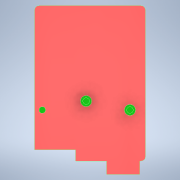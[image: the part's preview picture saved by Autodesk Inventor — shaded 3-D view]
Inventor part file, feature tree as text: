
AUTODESK INVENTOR PART (.ipt)
format: ipt  version: 2022 (Build 260153000, 153)  size: 167,424 bytes
history: native  units: mm
features: extrude x6, sketch x4, fillet x1
ambient origin geometry x8: Origin, YZ Plane, XZ Plane, XY Plane, X Axis, Y Axis, Z Axis, Center Point
bodies: Body1 (feature_tree)
feature tree (11):
  extrude  "Extrusion3"  Depth=70.0mm
  fillet  "Fillet1"  Radius=6.0mm
  sketch  "Sketch4"  dims[d14=2.0mm d16=18.5mm]
  extrude  "Extrusion5"  Depth=18.5mm
  extrude  "Extrusion6"  Depth=5.0mm
  extrude  "Extrusion7"  Depth=40.0mm TaperAngle=0.0deg
  extrude  "Extrusion8"  Depth=5.0mm
  extrude  "Extrusion9"  Depth=6.0mm
  sketch  "Sketch2"  dims[d0=50.0mm d1=70.0mm d12=6.0mm d13=0.0mm]
  sketch  "Sketch5"  dims[d17=5.0mm d31=5.0mm]
  sketch  "Sketch6"  dims[d34=3.0mm d37=40.0mm d38=0.0mm d41=5.0mm d44=19.75mm d45=19.75mm d46=7.0mm d48=5.6mm d49=0.0mm d50=3.0mm d51=34.4mm d52=0.0mm d53=10.64mm d54=0.0mm d55=3.0mm d56=29.36mm d57=0.0mm d58=2.5mm d59=15.0mm d60=6.0mm d61=23.0mm d62=27.0mm d63=23.0mm d4=0.0mm d5=0.0mm d6=0.0mm d7=0.0mm]
